# Revit family: Skystar_SK_32-E-2tr-MD600_RFA2018
name_source: partatom
category: Mechanical Equipment
revit_build: Autodesk Revit LT 2018 (Build: 20180329_1100(x64)
units: mm (PartAtom-declared; Revit-internal decimal feet)

## family parameters
Always vertical = Yes
Cut with Voids When Loaded = Yes
OmniClass Number = 23.75.00.00
OmniClass Title = Climate Control (HVAC)
Part Type = Normal
Room Calculation Point = Yes
Round Connector Dimension = Use Diameter
Shared = Yes
Work Plane-Based = Yes

## types (3) — shared parameters
4Tubi = No
A = 572 mm  [stored 1.87664 ft]
D_QC_IN = 15 mm  [stored 0.0492126 ft]
D_Q_C_OUT = 15 mm  [stored 0.0492126 ft]
Default Elevation = 1219 mm
Description = Kazetový fancoil
Filtro elettrostatico = No
Foro controsoffitto = 582 mm
Lato macchina = 572 mm  [stored 1.87664 ft]
Lookup Table Name = SABIANA-SkyStar
Manufacturer = Hydronix
Qpa = 0 m³/h
S = 348 mm
THIN_def = 50 °C
Type Comments = Výměník dvoutrubkový; elektrický ohřev; motor asynchronní 3-otáčkový; čelní deska, mřížka ocelový plech lakovaný  bílá RAL 9003
Type Image = md-600.jpg
URL = www.hydronix.cz
cpa = 1.0050 J/(g·°C)
cph = 4.1860 J/(g·°C)
rho_a = 1.2000 kg/m³
rho_h = 1000.2970 kg/m³
zero-valued in all types: BVc, COBie_Cost, COBie_ExpectedLife, COBie_ReplacementCost, COBie_WarrantyDurationLabour, COBie_WarrantyDurationParts

## per-type parameters (varying)
| type | Assembly Code | Model | Taglia |
| SK12-E MD | SK12-E (o.č.: 0079060)+MD600 (o.č.: 9079420) | SK 12-E MD | 12 |
| SK32-E MD | SK32-E (o.č.: 0079062)+MD600 (o.č.: 9079420) | SK32-E MD | 32 |
| SK22-E MD | SK22-E (o.č.: 0079061+MD600 (o.č.: 9079420) | SK22-E MD | 22 |

note: [stored X ft] marks values corroborated as IEEE doubles in the binary element streams (Revit-internal decimal feet)

## geometry (parser evidence)
native form markers: Blend x8
no freeform markers — native parametric forms only
